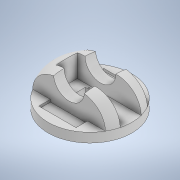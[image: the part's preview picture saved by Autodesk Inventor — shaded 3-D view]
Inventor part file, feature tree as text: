
AUTODESK INVENTOR PART (.ipt)
format: ipt  version: 2022 (Build 260153000, 153)  size: 241,152 bytes
history: native  units: mm
features: extrude x9, sketch x9, fillet x1
ambient origin geometry x8: Origin, YZ Plane, XZ Plane, XY Plane, X Axis, Y Axis, Z Axis, Center Point
bodies: Solid1 (feature_tree)
feature tree (19):
  extrude  "Extrusion1"  Depth=100.0mm TaperAngle=0.0deg
  extrude  "Extrusion2"  Depth=45.0mm
  extrude  "Extrusion3"  Depth=90.0mm
  extrude  "Extrusion4"  Depth=30.0mm
  extrude  "Extrusion5"  Depth=50.0mm TaperAngle=0.0deg
  fillet  "Fillet1"  Radius=20.0mm
  extrude  "Extrusion6"  Depth=15.0mm
  extrude  "Extrusion7"  Depth=10.0mm
  extrude  "Extrusion8"  Depth=137.75mm TaperAngle=0.0deg
  extrude  "Extrusion9"  Depth=5.0mm
  sketch  "Sketch1"  dims[d0=180.0mm d1=100.0mm d2=0.0mm]
  sketch  "Sketch2"  dims[d3=45.0mm d4=45.0mm]
  sketch  "Sketch3"  dims[d5=90.0mm d6=90.0mm]
  sketch  "Sketch4"  dims[d7=60.0mm d8=0.0mm d9=30.0mm]
  sketch  "Sketch5"  dims[d10=108.75mm d11=0.0mm d16=50.0mm d17=0.0mm d18=20.0mm d19=0.0mm]
  sketch  "Sketch6"  dims[d20=50.0mm d21=15.0mm]
  sketch  "Sketch7"  dims[d23=10.0mm d24=10.0mm]
  sketch  "Sketch10"  dims[d25=20.0mm d26=0.0mm d27=137.75mm d28=0.0mm]
  sketch  "Sketch11"  dims[d34=3.0mm d37=3.0mm d40=3.0mm d43=3.0mm d44=5.0mm d45=0.0mm d46=40.0mm d47=25.0mm d48=80.0mm d49=80.0mm d50=25.0mm d51=5.0mm d52=0.0mm]
